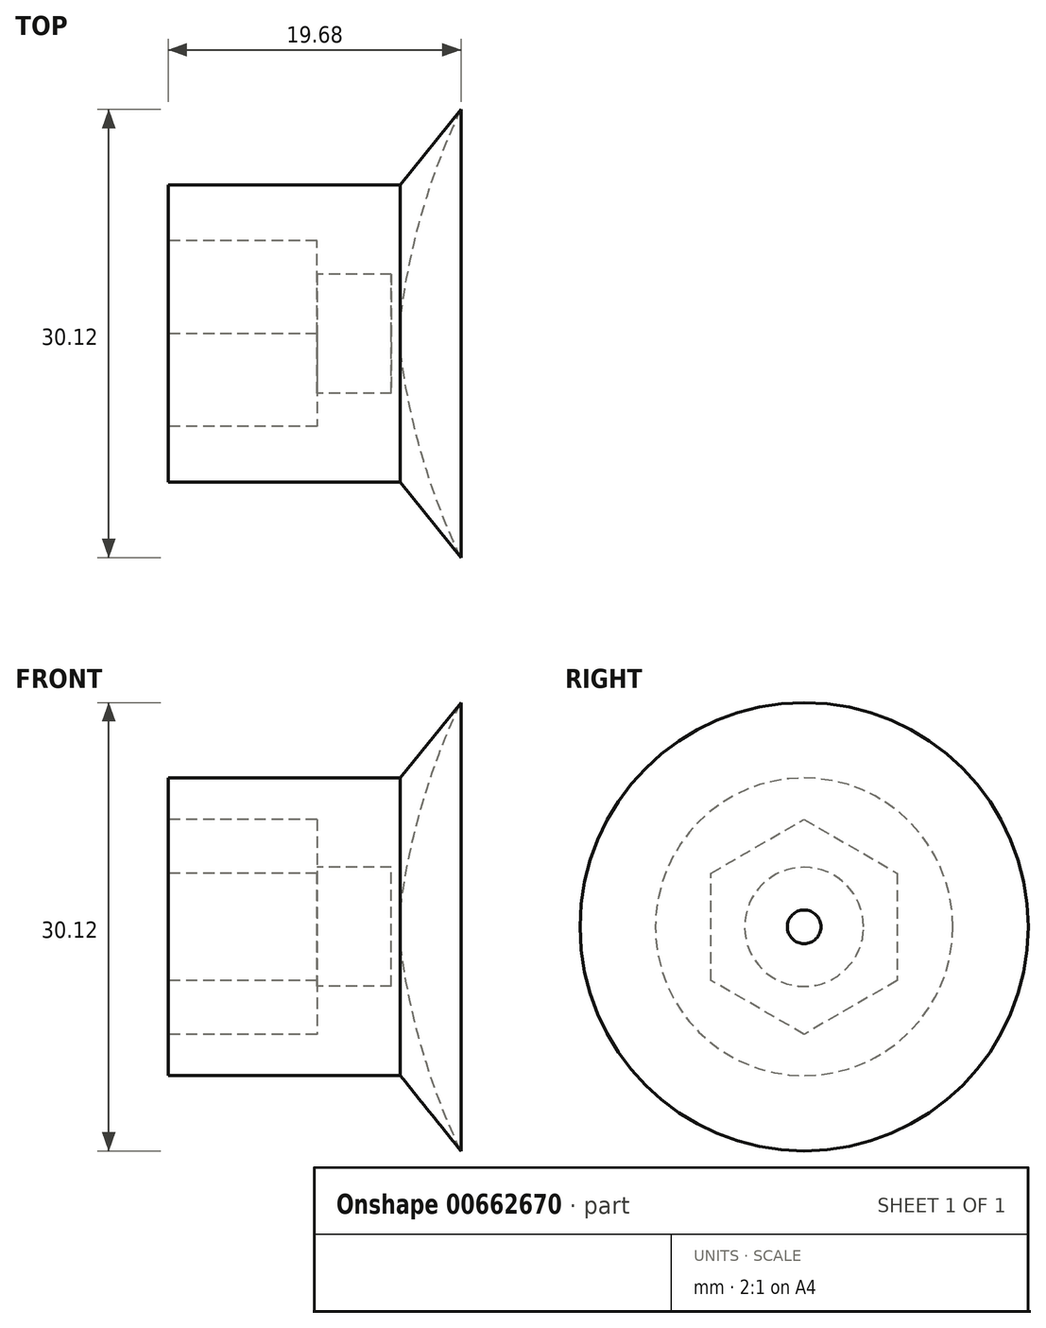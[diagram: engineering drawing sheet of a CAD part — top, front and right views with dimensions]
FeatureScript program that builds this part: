
annotation { "Feature Type Name" : "Feature", "Feature Type Description" : "" }
export const myFeature = defineFeature(function(context is Context, id is Id, definition is map)
    precondition{}
    {
        {
            var Q0;
            Q0=qCreatedBy(makeId("Right.planeOp"),FACE);
            var sketch = newSketch(context, id + "F0", { "sketchPlane" : qUnion([Q0])});
            skCircle(sketch, "E0", {"center": v(0, 0) * mm, "radius": 10 * mm});
            skCircle(sketch, "E1.cCircle", {"center": v(0, 0) * mm, "radius": 6.25 * mm, "construction": true});
            skLineSegment(sketch, "E1.0", {"start": v(6.25, 3.6) * mm, "end": v(6.25, -3.6) * mm});
            skLineSegment(sketch, "E1.1", {"start": v(6.25, -3.6) * mm, "end": v(0, -7.22) * mm});
            skLineSegment(sketch, "E1.2", {"start": v(0, -7.22) * mm, "end": v(-6.25, -3.6) * mm});
            skLineSegment(sketch, "E1.3", {"start": v(-6.25, -3.6) * mm, "end": v(-6.25, 3.6) * mm});
            skLineSegment(sketch, "E1.4", {"start": v(-6.25, 3.6) * mm, "end": v(0, 7.22) * mm});
            skLineSegment(sketch, "E1.5", {"start": v(0, 7.22) * mm, "end": v(6.25, 3.6) * mm});
            skPoint(sketch, "E1.0.midPoint", {"position": v(6.25, 0) * mm});
            skSolve(sketch);
        }
        {
            var Q0;
            Q0=makeQuery(id+"F0.imprint","IMPRINT",FACE,{"disambiguationData":[TD([[makeQuery(id+"F0.imprint","IMPRINT",EDGE,{"derivedFrom":sQuery(id+"F0.wireOp",EDGE,"E0")}),1.0]])]});
            extrude(context, id + "F1", {"entities" : qUnion([Q0]), "depth" : 10 * mm});
        }
        {
            var Q0;
            Q0=makeQuery(id+"F1.opExtrude","CAP_FACE",FACE,{"disambiguationData":[OSD([sQuery(id+"F0.wireOp",EDGE,"E0"),sQuery(id+"F0.wireOp",EDGE,"E1.0"),sQuery(id+"F0.wireOp",EDGE,"E1.1"),sQuery(id+"F0.wireOp",EDGE,"E1.2"),sQuery(id+"F0.wireOp",EDGE,"E1.3"),sQuery(id+"F0.wireOp",EDGE,"E1.4"),sQuery(id+"F0.wireOp",EDGE,"E1.5")])],"isStart":false});
            var sketch = newSketch(context, id + "F2", { "sketchPlane" : qUnion([Q0])});
            skCircle(sketch, "E2.0", {"center": v(0, 0) * mm, "radius": 10 * mm});
            skCircle(sketch, "E3", {"center": v(0, 0) * mm, "radius": 4 * mm});
            skSolve(sketch);
        }
        {
            var Q0;
            Q0=makeQuery(id+"F2.imprint","IMPRINT",FACE,{"disambiguationData":[TD([[makeQuery(id+"F2.imprint","IMPRINT",EDGE,{"derivedFrom":sQuery(id+"F2.wireOp",EDGE,"E3")}),-1.0]])]});
            var Q1;
            Q1=makeQuery(id+"F2.imprint","IMPRINT",FACE,{"disambiguationData":[TD([[makeQuery(id+"F2.imprint","IMPRINT",EDGE,{"derivedFrom":sQuery(id+"F2.wireOp",EDGE,"E2.0")}),1.0]])]});
            extrude(context, id + "F3", {"entities" : qUnion([Q0, Q1]), "operationType" : NewBodyOperationType.ADD, "depth" : 5 * mm});
        }
        {
            var Q0;
            Q0=makeQuery(id+"F3.opExtrude","CAP_FACE",FACE,{"disambiguationData":[OSD([sQuery(id+"F2.wireOp",EDGE,"E2.0"),sQuery(id+"F2.wireOp",EDGE,"E3")])],"isStart":false});
            var sketch = newSketch(context, id + "F4", { "sketchPlane" : qUnion([Q0])});
            skCircle(sketch, "E4.0", {"center": v(0, 0) * mm, "radius": 10 * mm});
            skSolve(sketch);
        }
        {
            var Q0;
            Q0=qSketchRegion(id+"F4",true);
            extrude(context, id + "F5", {"entities" : qUnion([Q0]), "operationType" : NewBodyOperationType.ADD, "depth" : .6 * mm});
        }
        {
            var Q0;
            Q0=qCreatedBy(makeId("Front.planeOp"),FACE);
            var sketch = newSketch(context, id + "F6", { "sketchPlane" : qUnion([Q0])});
            skLineSegment(sketch, "E5.0", {"start": v(15.6, 10) * mm, "end": v(15.6, -10) * mm});
            skLineSegment(sketch, "E6", {"start": v(15.6, -10) * mm, "end": v(19.68, -15.06) * mm});
            skLineSegment(sketch, "E7", {"start": v(0, 0) * mm, "end": v(22.2, 0) * mm});
            skArc(sketch, "E8", {"start": v(15.6, 10) * mm, "mid": v(15.84, -2.82) * mm, "end": v(19.68, -15.06) * mm});
            skSolve(sketch);
        }
        {
            var Q0;
            {var subQ0=sQuery(id+"F6.wireOp",EDGE,"E6");Q0=makeQuery(id+"F6.imprint","IMPRINT",FACE,{"disambiguationData":[TD([[makeQuery(id+"F6.imprint","IMPRINT",EDGE,{"derivedFrom":subQ0}),1.0]])]});}
            var Q1;
            Q1=sQuery(id+"F6.wireOp",EDGE,"E7");
            revolve(context, id + "F7", {"operationType" : NewBodyOperationType.ADD, "entities" : qUnion([Q0]), "axis" : qUnion([Q1]), "revolveType" : RevolveType.FULL});
        }
    });
